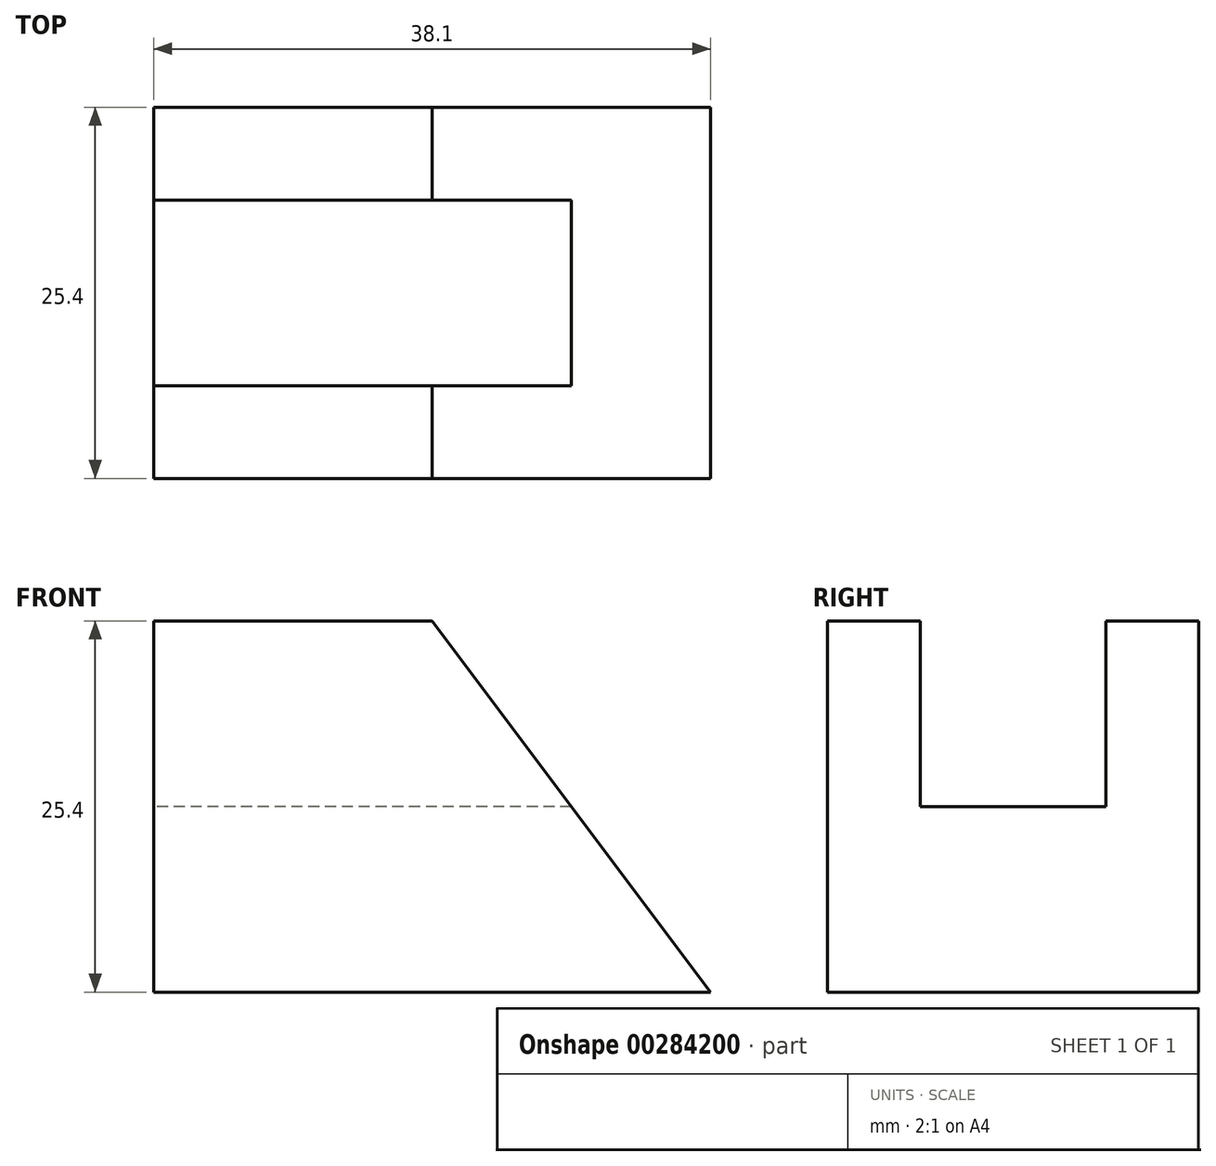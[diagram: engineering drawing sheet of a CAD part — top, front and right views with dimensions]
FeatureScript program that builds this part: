
annotation { "Feature Type Name" : "Feature", "Feature Type Description" : "" }
export const myFeature = defineFeature(function(context is Context, id is Id, definition is map)
    precondition{}
    {
        {
            var Q0;
            Q0=qCreatedBy(makeId("Front.planeOp"),FACE);
            var sketch = newSketch(context, id + "F0", { "sketchPlane" : qUnion([Q0])});
            skLineSegment(sketch, "E0", {"start": v(0, 0) * mm, "end": v(0, 25.4) * mm});
            skLineSegment(sketch, "E1", {"start": v(0, 25.4) * mm, "end": v(19.05, 25.4) * mm});
            skLineSegment(sketch, "E2", {"start": v(19.05, 25.4) * mm, "end": v(38.1, 0) * mm});
            skLineSegment(sketch, "E3", {"start": v(38.1, 0) * mm, "end": v(0, 0) * mm});
            skSolve(sketch);
        }
        {
            var Q0;
            Q0=makeQuery(id+"F0.imprint","IMPRINT",FACE,{"disambiguationData":[TD([[makeQuery(id+"F0.imprint","IMPRINT",EDGE,{"derivedFrom":sQuery(id+"F0.wireOp",EDGE,"E0")}),-1.0]])]});
            extrude(context, id + "F1", {"entities" : qUnion([Q0]), "depth" : 25.4 * mm});
        }
        {
            var Q0;
            Q0=makeQuery(id+"F1.opExtrude","SWEPT_FACE",FACE,{"disambiguationData":[OSD([sQuery(id+"F0.wireOp",EDGE,"E0")])]});
            var sketch = newSketch(context, id + "F2", { "sketchPlane" : qUnion([Q0])});
            skLineSegment(sketch, "E4", {"start": v(0, 25.4) * mm, "end": v(6.35, 25.4) * mm});
            skLineSegment(sketch, "E5", {"start": v(6.35, 25.4) * mm, "end": v(6.35, 12.7) * mm});
            skLineSegment(sketch, "E6", {"start": v(6.35, 12.7) * mm, "end": v(19.05, 12.7) * mm});
            skLineSegment(sketch, "E7", {"start": v(19.05, 12.7) * mm, "end": v(19.05, 25.4) * mm});
            skLineSegment(sketch, "E8", {"start": v(19.05, 25.4) * mm, "end": v(25.4, 25.4) * mm});
            skSolve(sketch);
        }
        {
            var Q0;
            {var subQ0=sQuery(id+"F2.wireOp",EDGE,"E5");Q0=makeQuery(id+"F2.imprint","IMPRINT",FACE,{"disambiguationData":[TD([[makeQuery(id+"F2.imprint","IMPRINT",EDGE,{"derivedFrom":subQ0}),1.0]])]});}
            extrude(context, id + "F3", {"entities" : qUnion([Q0]), "operationType" : NewBodyOperationType.REMOVE, "endBound" : BoundingType.THROUGH_ALL, "oppositeDirection" : true, "depth" : 25.4 * mm});
        }
    });
